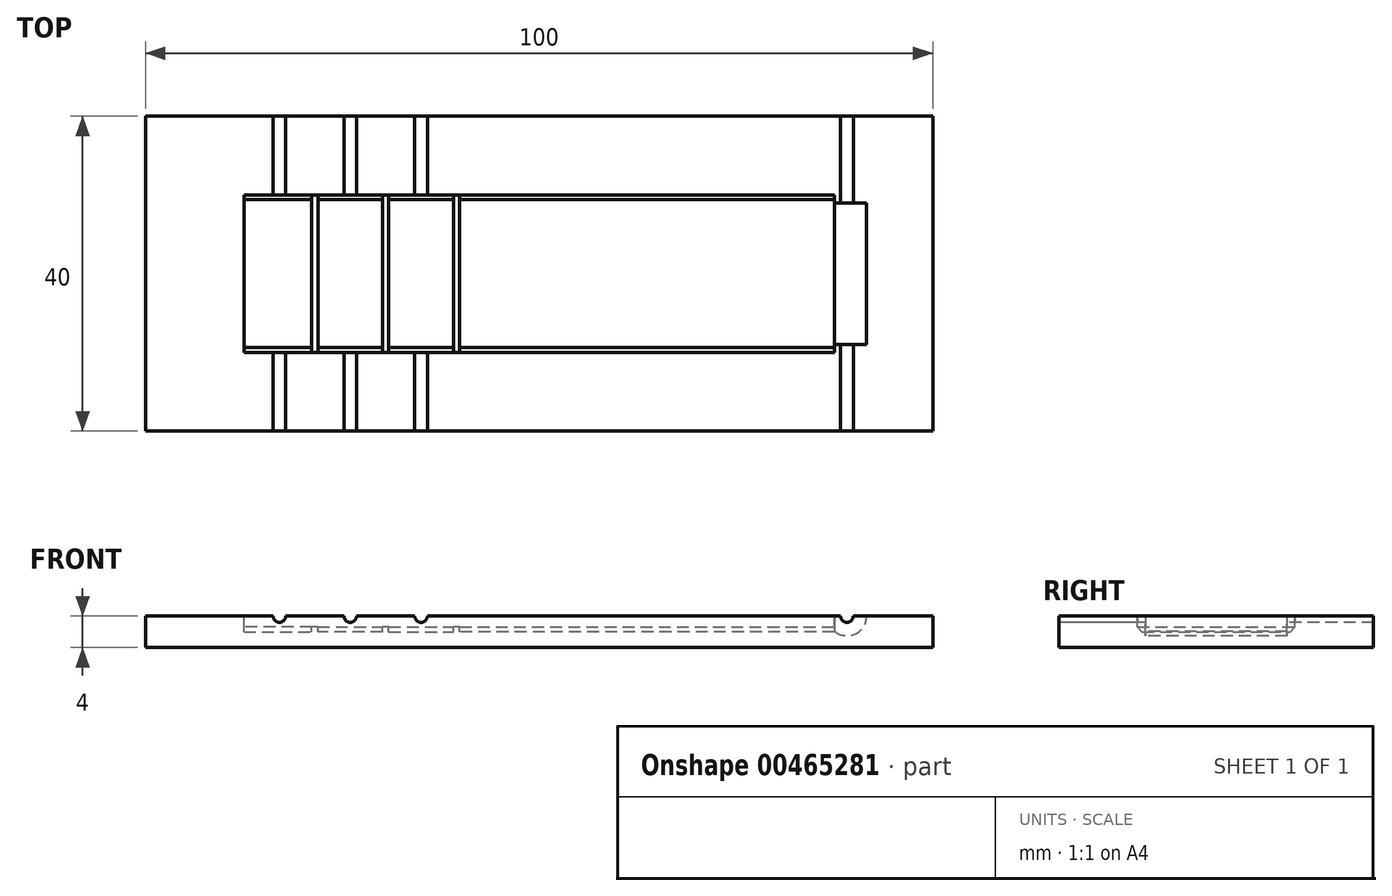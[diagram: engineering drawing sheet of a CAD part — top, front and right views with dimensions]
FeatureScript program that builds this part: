
annotation { "Feature Type Name" : "Feature", "Feature Type Description" : "" }
export const myFeature = defineFeature(function(context is Context, id is Id, definition is map)
    precondition{}
    {
        {
            var Q0;
            Q0=qCreatedBy(makeId("Top.planeOp"),FACE);
            var sketch = newSketch(context, id + "F0", { "sketchPlane" : qUnion([Q0])});
            skLineSegment(sketch, "E0.bottom", {"start": v(50, -20) * mm, "end": v(-50, -20) * mm});
            skLineSegment(sketch, "E0.top", {"start": v(50, 20) * mm, "end": v(-50, 20) * mm});
            skLineSegment(sketch, "E0.left", {"start": v(50, -20) * mm, "end": v(50, 20) * mm});
            skLineSegment(sketch, "E0.right", {"start": v(-50, -20) * mm, "end": v(-50, 20) * mm});
            skPoint(sketch, "E0.middle", {"position": v(0, 0) * mm});
            skSolve(sketch);
        }
        {
            var Q0;
            Q0=makeQuery(id+"F0.imprint","IMPRINT",FACE,{"disambiguationData":[TD([[makeQuery(id+"F0.imprint","IMPRINT",EDGE,{"derivedFrom":sQuery(id+"F0.wireOp",EDGE,"E0.bottom")}),-1.0]])]});
            extrude(context, id + "F1", {"entities" : qUnion([Q0]), "depth" : 4 * mm});
        }
        {
            var Q0;
            Q0=makeQuery(id+"F1.opExtrude","CAP_FACE",FACE,{"disambiguationData":[OSD([sQuery(id+"F0.wireOp",EDGE,"E0.bottom"),sQuery(id+"F0.wireOp",EDGE,"E0.top"),sQuery(id+"F0.wireOp",EDGE,"E0.left"),sQuery(id+"F0.wireOp",EDGE,"E0.right")])],"isStart":false});
            var sketch = newSketch(context, id + "F2", { "sketchPlane" : qUnion([Q0])});
            skLineSegment(sketch, "E1.bottom", {"start": v(37.5, -10) * mm, "end": v(-37.5, -10) * mm});
            skLineSegment(sketch, "E1.top", {"start": v(37.5, 10) * mm, "end": v(-37.5, 10) * mm});
            skLineSegment(sketch, "E1.left", {"start": v(37.5, -10) * mm, "end": v(37.5, 10) * mm});
            skLineSegment(sketch, "E1.right", {"start": v(-37.5, -10) * mm, "end": v(-37.5, 10) * mm});
            skPoint(sketch, "E1.middle", {"position": v(0, 0) * mm});
            skSolve(sketch);
        }
        {
            var Q0;
            Q0=makeQuery(id+"F2.imprint","IMPRINT",FACE,{"disambiguationData":[TD([[makeQuery(id+"F2.imprint","IMPRINT",EDGE,{"derivedFrom":sQuery(id+"F2.wireOp",EDGE,"E1.bottom")}),-1.0]])]});
            extrude(context, id + "F3", {"entities" : qUnion([Q0]), "operationType" : NewBodyOperationType.REMOVE, "oppositeDirection" : true, "depth" : 2 * mm});
        }
        {
            var Q0;
            Q0=makeQuery(id+"F1.opExtrude","SWEPT_FACE",FACE,{"disambiguationData":[OSD([sQuery(id+"F0.wireOp",EDGE,"E0.bottom")])]});
            var sketch = newSketch(context, id + "F4", { "sketchPlane" : qUnion([Q0])});
            skCircle(sketch, "E2", {"center": v(-33, 4) * mm, "radius": 0.8 * mm});
            skCircle(sketch, "E3", {"center": v(-24, 4) * mm, "radius": 0.8 * mm});
            skCircle(sketch, "E4", {"center": v(-15, 4) * mm, "radius": 0.8 * mm});
            skCircle(sketch, "E5", {"center": v(39.1, 4) * mm, "radius": 0.8 * mm});
            skSolve(sketch);
        }
        {
            var Q0;
            Q0=qCreatedBy(makeId("Front.planeOp"),FACE);
            var sketch = newSketch(context, id + "F5", { "sketchPlane" : qUnion([Q0])});
            skCircle(sketch, "E6", {"center": v(39.1, 4) * mm, "radius": 2.5 * mm});
            skSolve(sketch);
        }
        {
            var Q0;
            Q0=makeQuery(id+"F5.imprint","IMPRINT",FACE,{"disambiguationData":[TD([[makeQuery(id+"F5.imprint","IMPRINT",EDGE,{"derivedFrom":sQuery(id+"F5.wireOp",EDGE,"E6")}),1.0]])]});
            extrude(context, id + "F6", {"entities" : qUnion([Q0]), "operationType" : NewBodyOperationType.REMOVE, "endBound" : BoundingType.SYMMETRIC, "oppositeDirection" : true, "depth" : 18 * mm});
        }
        {
            var Q0;
            {var subQ0=sQuery(id+"F4.wireOp",EDGE,"E2");var subQ1=makeQuery(id+"F1.opExtrude","CAP_EDGE",EDGE,{"disambiguationData":[OSD([sQuery(id+"F0.wireOp",EDGE,"E0.bottom")])],"isStart":false});var subQ2=makeQuery(id+"F4.imprint","INTERSECT",VERTEX,{"disambiguationData":[OD(0.0)],"derivedFrom":[subQ1,subQ0]});Q0=makeQuery(id+"F4.imprint","IMPRINT",FACE,{"disambiguationData":[TD([[makeQuery(id+"F4.imprint","IMPRINT",EDGE,{"disambiguationData":[TD([[subQ2,-1.0]])],"derivedFrom":subQ0}),1.0]])]});}
            var Q1;
            {var subQ0=sQuery(id+"F4.wireOp",EDGE,"E3");var subQ1=makeQuery(id+"F1.opExtrude","CAP_EDGE",EDGE,{"disambiguationData":[OSD([sQuery(id+"F0.wireOp",EDGE,"E0.bottom")])],"isStart":false});var subQ2=makeQuery(id+"F4.imprint","INTERSECT",VERTEX,{"disambiguationData":[OD(0.0)],"derivedFrom":[subQ1,subQ0]});Q1=makeQuery(id+"F4.imprint","IMPRINT",FACE,{"disambiguationData":[TD([[makeQuery(id+"F4.imprint","IMPRINT",EDGE,{"disambiguationData":[TD([[subQ2,-1.0]])],"derivedFrom":subQ0}),1.0]])]});}
            var Q2;
            {var subQ0=sQuery(id+"F4.wireOp",EDGE,"E4");var subQ1=makeQuery(id+"F1.opExtrude","CAP_EDGE",EDGE,{"disambiguationData":[OSD([sQuery(id+"F0.wireOp",EDGE,"E0.bottom")])],"isStart":false});var subQ2=makeQuery(id+"F4.imprint","INTERSECT",VERTEX,{"disambiguationData":[OD(0.0)],"derivedFrom":[subQ1,subQ0]});Q2=makeQuery(id+"F4.imprint","IMPRINT",FACE,{"disambiguationData":[TD([[makeQuery(id+"F4.imprint","IMPRINT",EDGE,{"disambiguationData":[TD([[subQ2,1.0]])],"derivedFrom":subQ0}),1.0]])]});}
            var Q3;
            {var subQ0=sQuery(id+"F4.wireOp",EDGE,"E5");var subQ1=makeQuery(id+"F1.opExtrude","CAP_EDGE",EDGE,{"disambiguationData":[OSD([sQuery(id+"F0.wireOp",EDGE,"E0.bottom")])],"isStart":false});var subQ2=makeQuery(id+"F4.imprint","INTERSECT",VERTEX,{"disambiguationData":[OD(0.0)],"derivedFrom":[subQ1,subQ0]});Q3=makeQuery(id+"F4.imprint","IMPRINT",FACE,{"disambiguationData":[TD([[makeQuery(id+"F4.imprint","IMPRINT",EDGE,{"disambiguationData":[TD([[subQ2,1.0]])],"derivedFrom":subQ0}),1.0]])]});}
            extrude(context, id + "F7", {"entities" : qUnion([Q0, Q1, Q2, Q3]), "operationType" : NewBodyOperationType.REMOVE, "endBound" : BoundingType.THROUGH_ALL, "oppositeDirection" : true, "depth" : 25 * mm});
        }
        {
            var Q0;
            Q0=makeQuery(id+"F3.boolean.opBoolean","COPY",FACE,{"derivedFrom":makeQuery(id+"F3.opExtrude","CAP_FACE",FACE,{"disambiguationData":[OSD([sQuery(id+"F2.wireOp",EDGE,"E1.bottom"),sQuery(id+"F2.wireOp",EDGE,"E1.top"),sQuery(id+"F2.wireOp",EDGE,"E1.left"),sQuery(id+"F2.wireOp",EDGE,"E1.right")])],"isStart":false})});
            var sketch = newSketch(context, id + "F8", { "sketchPlane" : qUnion([Q0])});
            skLineSegment(sketch, "E7.bottom", {"start": v(-19.1, -10) * mm, "end": v(-19.9, -10) * mm});
            skLineSegment(sketch, "E7.top", {"start": v(-19.1, 10) * mm, "end": v(-19.9, 10) * mm});
            skLineSegment(sketch, "E7.left", {"start": v(-19.1, -10) * mm, "end": v(-19.1, 10) * mm});
            skLineSegment(sketch, "E7.right", {"start": v(-19.9, -10) * mm, "end": v(-19.9, 10) * mm});
            skPoint(sketch, "E7.middle", {"position": v(-19.5, 0) * mm});
            skLineSegment(sketch, "E8.bottom", {"start": v(-28.1, -10) * mm, "end": v(-28.9, -10) * mm});
            skLineSegment(sketch, "E8.top", {"start": v(-28.1, 10) * mm, "end": v(-28.9, 10) * mm});
            skLineSegment(sketch, "E8.left", {"start": v(-28.1, -10) * mm, "end": v(-28.1, 10) * mm});
            skLineSegment(sketch, "E8.right", {"start": v(-28.9, -10) * mm, "end": v(-28.9, 10) * mm});
            skPoint(sketch, "E8.middle", {"position": v(-28.5, 0) * mm});
            skLineSegment(sketch, "E9.bottom", {"start": v(-10.1, -10) * mm, "end": v(-10.9, -10) * mm});
            skLineSegment(sketch, "E9.top", {"start": v(-10.1, 10) * mm, "end": v(-10.9, 10) * mm});
            skLineSegment(sketch, "E9.left", {"start": v(-10.1, -10) * mm, "end": v(-10.1, 10) * mm});
            skLineSegment(sketch, "E9.right", {"start": v(-10.9, -10) * mm, "end": v(-10.9, 10) * mm});
            skPoint(sketch, "E9.middle", {"position": v(-10.5, 0) * mm});
            skSolve(sketch);
        }
        {
            var Q0;
            Q0=makeQuery(id+"F3.boolean.opBoolean","COPY",EDGE,{"derivedFrom":makeQuery(id+"F3.opExtrude","CAP_EDGE",EDGE,{"disambiguationData":[OSD([sQuery(id+"F2.wireOp",EDGE,"E1.top")])],"isStart":false})});
            var Q1;
            Q1=makeQuery(id+"F3.boolean.opBoolean","COPY",EDGE,{"derivedFrom":makeQuery(id+"F3.opExtrude","CAP_EDGE",EDGE,{"disambiguationData":[OSD([sQuery(id+"F2.wireOp",EDGE,"E1.bottom")])],"isStart":false})});
            chamfer(context, id + "F9", {"entities" : qUnion([Q0, Q1]), "width" : .6 * mm, "tangentPropagation" : true});
        }
        {
            var Q0;
            Q0=makeQuery(id+"F8.imprint","IMPRINT",FACE,{"disambiguationData":[TD([[makeQuery(id+"F8.imprint","IMPRINT",EDGE,{"derivedFrom":sQuery(id+"F8.wireOp",EDGE,"E8.bottom")}),-1.0]])]});
            var Q1;
            Q1=makeQuery(id+"F8.imprint","IMPRINT",FACE,{"disambiguationData":[TD([[makeQuery(id+"F8.imprint","IMPRINT",EDGE,{"derivedFrom":sQuery(id+"F8.wireOp",EDGE,"E7.bottom")}),-1.0]])]});
            var Q2;
            Q2=makeQuery(id+"F8.imprint","IMPRINT",FACE,{"disambiguationData":[TD([[makeQuery(id+"F8.imprint","IMPRINT",EDGE,{"derivedFrom":sQuery(id+"F8.wireOp",EDGE,"E9.bottom")}),-1.0]])]});
            extrude(context, id + "F10", {"entities" : qUnion([Q0, Q1, Q2]), "operationType" : NewBodyOperationType.ADD, "depth" : .6 * mm});
        }
    });
